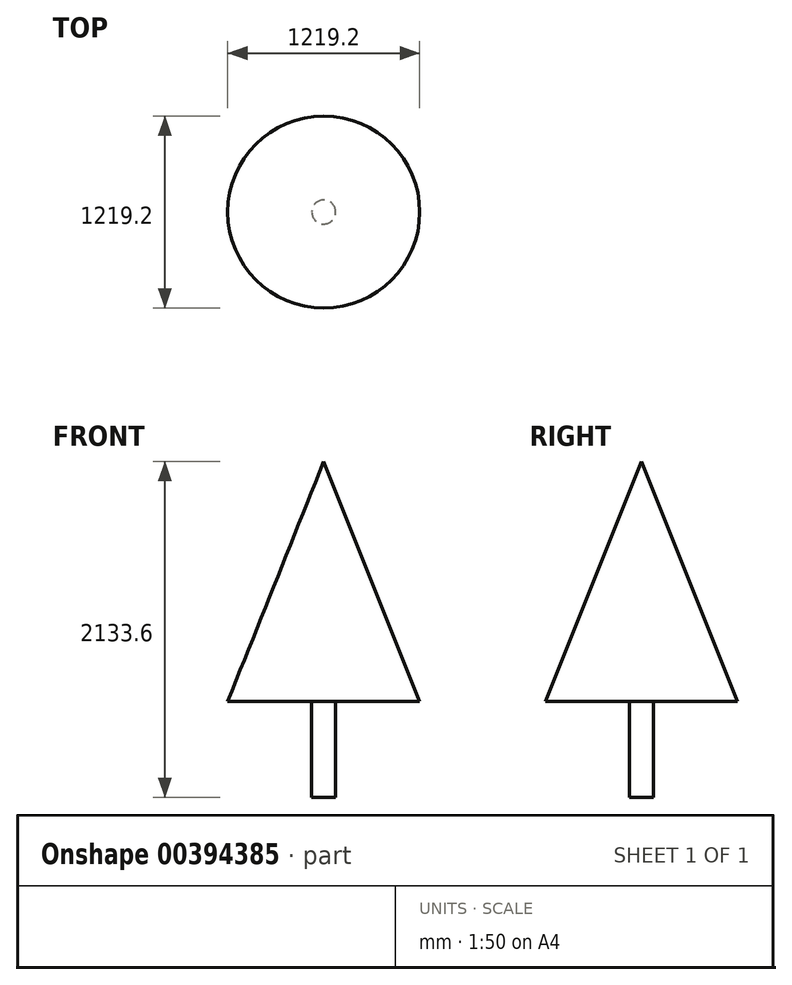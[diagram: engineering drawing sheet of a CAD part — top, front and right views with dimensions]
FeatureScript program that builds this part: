
annotation { "Feature Type Name" : "Feature", "Feature Type Description" : "" }
export const myFeature = defineFeature(function(context is Context, id is Id, definition is map)
    precondition{}
    {
        {
            var Q0;
            Q0=qCreatedBy(makeId("Right.planeOp"),FACE);
            var sketch = newSketch(context, id + "F0", { "sketchPlane" : qUnion([Q0])});
            skLineSegment(sketch, "E0", {"start": v(0, 0) * mm, "end": v(0, 1524) * mm});
            skLineSegment(sketch, "E1", {"start": v(0, 0) * mm, "end": v(-609.6, 0) * mm});
            skLineSegment(sketch, "E2", {"start": v(-609.6, 0) * mm, "end": v(0, 1524) * mm});
            skSolve(sketch);
        }
        {
            var Q0;
            Q0=makeQuery(id+"F0.imprint","IMPRINT",FACE,{"disambiguationData":[TD([[makeQuery(id+"F0.imprint","IMPRINT",EDGE,{"derivedFrom":sQuery(id+"F0.wireOp",EDGE,"E0")}),1.0]])]});
            var Q1;
            Q1=sQuery(id+"F0.wireOp",EDGE,"E0");
            revolve(context, id + "F1", {"entities" : qUnion([Q0]), "axis" : qUnion([Q1]), "revolveType" : RevolveType.FULL});
        }
        {
            var Q0;
            Q0=makeQuery(id+"F1.opRevolve","SWEPT_FACE",FACE,{"disambiguationData":[OSD([sQuery(id+"F0.wireOp",EDGE,"E1")])]});
            var sketch = newSketch(context, id + "F2", { "sketchPlane" : qUnion([Q0])});
            skCircle(sketch, "E3", {"center": v(0, 0) * mm, "radius": 76.2 * mm});
            skSolve(sketch);
        }
        {
            var Q0;
            Q0=makeQuery(id+"F2.imprint","IMPRINT",FACE,{"disambiguationData":[TD([[makeQuery(id+"F2.imprint","IMPRINT",EDGE,{"derivedFrom":sQuery(id+"F2.wireOp",EDGE,"E3")}),1.0]])]});
            extrude(context, id + "F3", {"entities" : qUnion([Q0]), "operationType" : NewBodyOperationType.ADD, "depth" : 609.6 * mm});
        }
    });
